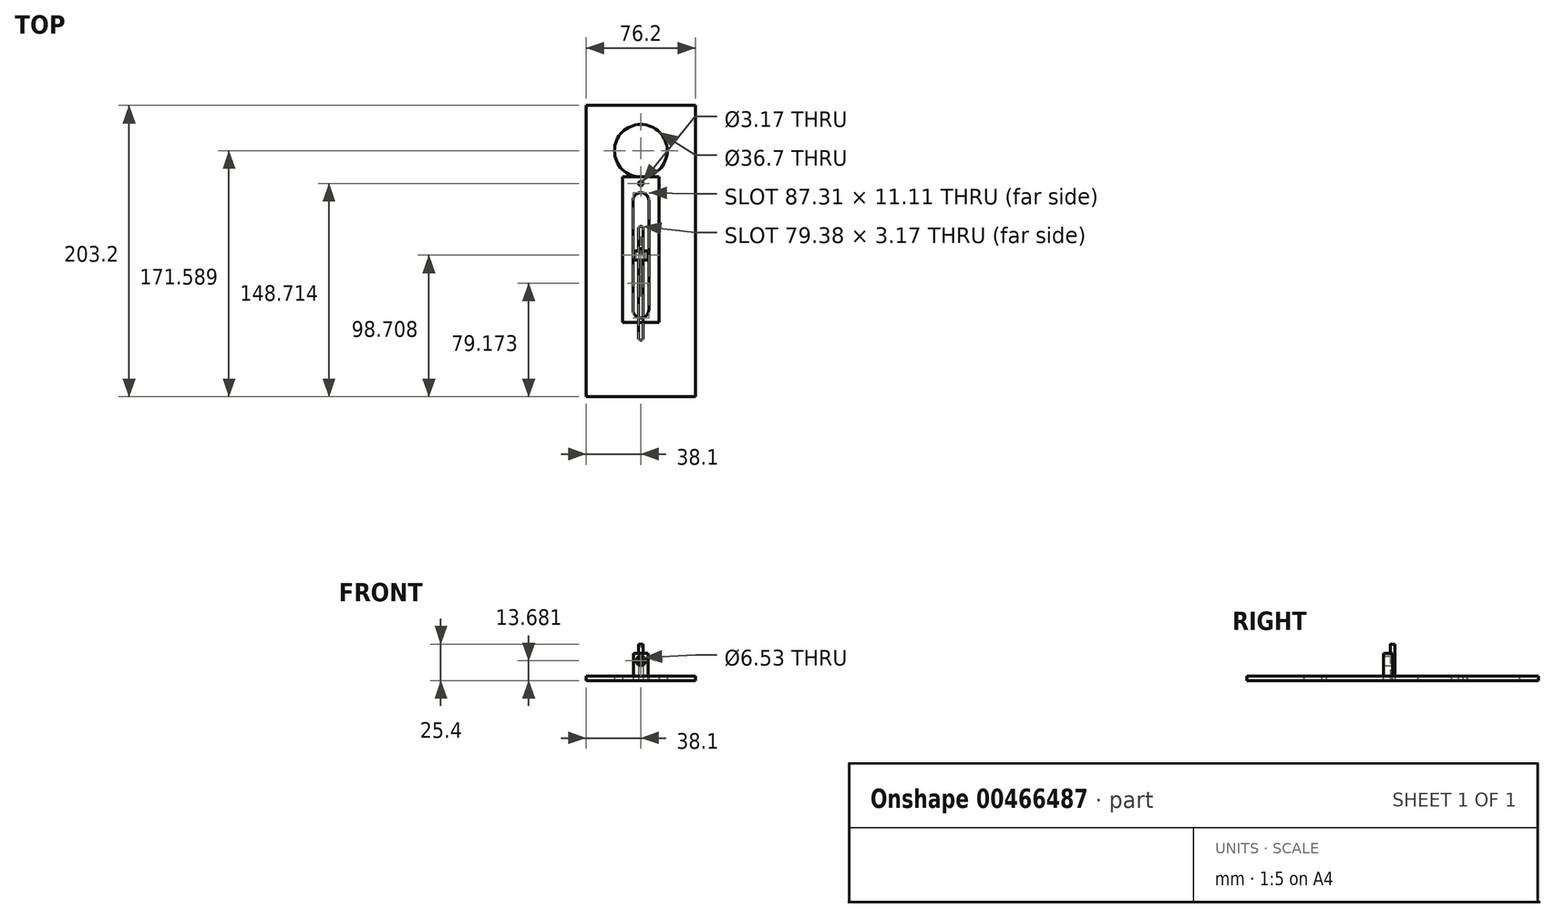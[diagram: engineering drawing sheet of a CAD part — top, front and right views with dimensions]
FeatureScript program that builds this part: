
annotation { "Feature Type Name" : "Feature", "Feature Type Description" : "" }
export const myFeature = defineFeature(function(context is Context, id is Id, definition is map)
    precondition{}
    {
        {
            var Q0;
            Q0=qCreatedBy(makeId("Top.planeOp"),FACE);
            var sketch = newSketch(context, id + "F0", { "sketchPlane" : qUnion([Q0])});
            skLineSegment(sketch, "E0.bottom", {"start": v(-38.1, 101.6) * mm, "end": v(38.1, 101.6) * mm});
            skLineSegment(sketch, "E0.top", {"start": v(-38.1, -101.6) * mm, "end": v(38.1, -101.6) * mm});
            skLineSegment(sketch, "E0.left", {"start": v(-38.1, 101.6) * mm, "end": v(-38.1, -101.6) * mm});
            skLineSegment(sketch, "E0.right", {"start": v(38.1, 101.6) * mm, "end": v(38.1, -101.6) * mm});
            skArc(sketch, "E1", {"start": v(1.59, 15.67) * mm, "mid": v(0, 17.26) * mm, "end": v(-1.59, 15.67) * mm});
            skArc(sketch, "E2", {"start": v(-1.59, -60.53) * mm, "mid": v(0, -62.11) * mm, "end": v(1.59, -60.53) * mm});
            skLineSegment(sketch, "E3", {"start": v(-1.59, 15.67) * mm, "end": v(-1.59, -60.53) * mm});
            skLineSegment(sketch, "E4", {"start": v(1.59, 15.67) * mm, "end": v(1.59, -60.53) * mm});
            skCircle(sketch, "E5", {"center": v(0, 69.99) * mm, "radius": 18.35 * mm});
            skSolve(sketch);
        }
        {
            var Q0;
            Q0=makeQuery(id+"F0.imprint","IMPRINT",FACE,{"disambiguationData":[TD([[makeQuery(id+"F0.imprint","IMPRINT",EDGE,{"derivedFrom":sQuery(id+"F0.wireOp",EDGE,"E0.bottom")}),-1.0]])]});
            extrude(context, id + "F1", {"entities" : qUnion([Q0]), "depth" : 3.17 * mm});
        }
        {
            var Q0;
            Q0=qCreatedBy(makeId("Top.planeOp"),FACE);
            var sketch = newSketch(context, id + "F2", { "sketchPlane" : qUnion([Q0])});
            skLineSegment(sketch, "E6.bottom", {"start": v(-12.7, 51.88) * mm, "end": v(12.7, 51.88) * mm});
            skLineSegment(sketch, "E6.top", {"start": v(-12.7, -49.72) * mm, "end": v(12.7, -49.72) * mm});
            skLineSegment(sketch, "E6.left", {"start": v(-12.7, 51.88) * mm, "end": v(-12.7, -49.72) * mm});
            skLineSegment(sketch, "E6.right", {"start": v(12.7, 51.88) * mm, "end": v(12.7, -49.72) * mm});
            skCircle(sketch, "E7", {"center": v(0, 47.11) * mm, "radius": 1.59 * mm});
            skArc(sketch, "E8", {"start": v(5.56, 35.2) * mm, "mid": v(0, 40.76) * mm, "end": v(-5.56, 35.2) * mm});
            skArc(sketch, "E9", {"start": v(-5.56, -41) * mm, "mid": v(0, -46.55) * mm, "end": v(5.56, -41) * mm});
            skLineSegment(sketch, "E10", {"start": v(-5.56, 35.2) * mm, "end": v(-5.56, -41) * mm});
            skLineSegment(sketch, "E11", {"start": v(5.56, -41) * mm, "end": v(5.56, 35.2) * mm});
            skSolve(sketch);
        }
        {
            var Q0;
            Q0=makeQuery(id+"F2.imprint","IMPRINT",FACE,{"disambiguationData":[TD([[makeQuery(id+"F2.imprint","IMPRINT",EDGE,{"derivedFrom":sQuery(id+"F2.wireOp",EDGE,"E6.bottom")}),-1.0]])]});
            extrude(context, id + "F3", {"entities" : qUnion([Q0]), "depth" : 3.17 * mm});
        }
        {
            var Q0;
            Q0=qCreatedBy(makeId("Top.planeOp"),FACE);
            var sketch = newSketch(context, id + "F4", { "sketchPlane" : qUnion([Q0])});
            skCircle(sketch, "E12", {"center": v(0, 0) * mm, "radius": 1.59 * mm});
            skSolve(sketch);
        }
        {
            var Q0;
            Q0 = qSketchRegion(id + "F4", true);
            extrude(context, id + "F5", {"entities" : qUnion([Q0]), "depth" : 25.4 * mm});
        }
        {
            var Q0;
            Q0=qCreatedBy(makeId("Front.planeOp"),FACE);
            var sketch = newSketch(context, id + "F6", { "sketchPlane" : qUnion([Q0])});
            skLineSegment(sketch, "E13.bottom", {"start": v(-5.05, 0) * mm, "end": v(5.05, 0) * mm});
            skLineSegment(sketch, "E13.top", {"start": v(-5.05, 19.05) * mm, "end": v(5.05, 19.05) * mm});
            skLineSegment(sketch, "E13.left", {"start": v(-5.05, 0) * mm, "end": v(-5.05, 19.05) * mm});
            skLineSegment(sketch, "E13.right", {"start": v(5.05, 0) * mm, "end": v(5.05, 19.05) * mm});
            skPoint(sketch, "E14", {"position": v(-5.05, 0) * mm});
            skCircle(sketch, "E15", {"center": v(0, 13.68) * mm, "radius": 3.97 * mm, "construction": true});
            skSolve(sketch);
        }
        {
            var Q0;
            Q0=makeQuery(id+"F6.imprint","IMPRINT",FACE,{"disambiguationData":[TD([[makeQuery(id+"F6.imprint","IMPRINT",EDGE,{"derivedFrom":sQuery(id+"F6.wireOp",EDGE,"E13.bottom")}),1.0]])]});
            extrude(context, id + "F7", {"entities" : qUnion([Q0]), "depth" : 6.35 * mm});
        }
        {
            var Q0;
            Q0=sQuery(id+"F6.wireOp",VERTEX,"E15.center");
            var Q1;
            Q1=makeQuery(id+"F7.opExtrude","SWEPT_BODY",BODY,{"disambiguationData":[OSD([sQuery(id+"F6.wireOp",EDGE,"E13.bottom"),sQuery(id+"F6.wireOp",EDGE,"E13.top"),sQuery(id+"F6.wireOp",EDGE,"E13.left"),sQuery(id+"F6.wireOp",EDGE,"E13.right")])]});
            hole(context, id + "F8", {"style" : HoleStyle.SIMPLE, "endStyle" : HoleEndStyle.THROUGH, "oppositeDirection" : true, "standardTappedOrClearance" : lookupTablePath({ "standard" : "ANSI", "engagement" : "75%", "pitch" : "18 tpi", "size" : "5/16", "type" : "Tapped" }), "standardBlindInLast" : lookupTablePath({ "standard" : "ANSI", "engagement" : "75%", "pitch" : "18 tpi", "size" : "5/16", "type" : "Tapped" }), "holeDiameter" : 6.53 * mm, "showTappedDepth" : true, "isTappedThrough" : true, "tappedDepth" : 12.7 * mm, "tapClearance" : 3, "locations" : qUnion([Q0]), "scope" : qUnion([Q1]), "majorDiameter" : 7.94 * mm});
        }
    });
